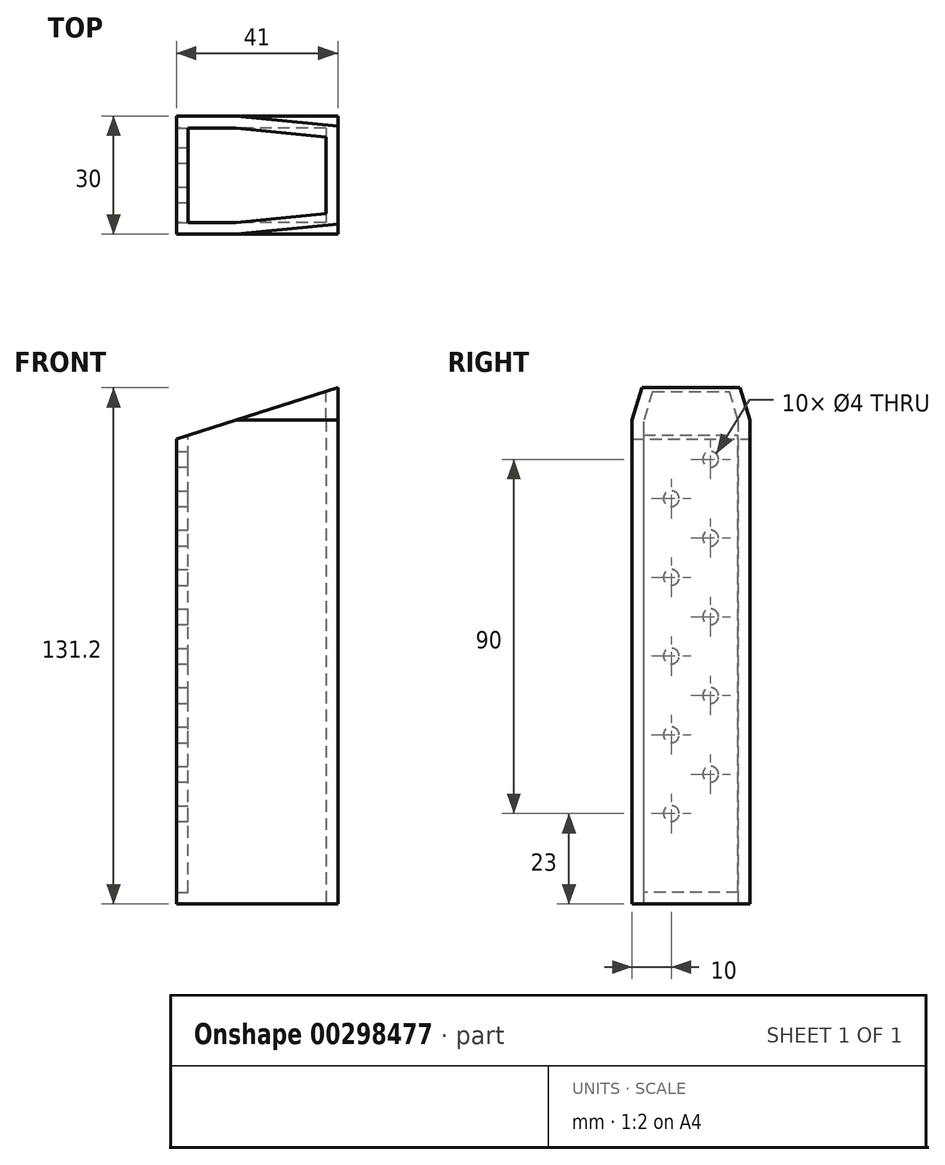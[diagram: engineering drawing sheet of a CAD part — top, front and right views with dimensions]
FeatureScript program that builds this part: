
annotation { "Feature Type Name" : "Feature", "Feature Type Description" : "" }
export const myFeature = defineFeature(function(context is Context, id is Id, definition is map)
    precondition{}
    {
        {
            var Q0;
            Q0=qCreatedBy(makeId("Right.planeOp"),FACE);
            var sketch = newSketch(context, id + "F0", { "sketchPlane" : qUnion([Q0])});
            skLineSegment(sketch, "E0", {"start": v(10, 10) * mm, "end": v(0, 20) * mm});
            skLineSegment(sketch, "E1", {"start": v(0, 20) * mm, "end": v(10, 30) * mm});
            skLineSegment(sketch, "E2", {"start": v(10, 30) * mm, "end": v(0, 40) * mm});
            skLineSegment(sketch, "E3", {"start": v(0, 40) * mm, "end": v(10, 50) * mm});
            skLineSegment(sketch, "E4", {"start": v(10, 50) * mm, "end": v(0, 60) * mm});
            skLineSegment(sketch, "E5", {"start": v(0, 60) * mm, "end": v(10, 70) * mm});
            skLineSegment(sketch, "E6", {"start": v(10, 70) * mm, "end": v(0, 80) * mm});
            skLineSegment(sketch, "E7", {"start": v(0, 80) * mm, "end": v(10, 90) * mm});
            skLineSegment(sketch, "E8", {"start": v(10, 90) * mm, "end": v(0, 100) * mm});
            skCircle(sketch, "E9", {"center": v(10, 90) * mm, "radius": 2 * mm});
            skCircle(sketch, "E10", {"center": v(0, 80) * mm, "radius": 2 * mm});
            skCircle(sketch, "E11", {"center": v(10, 70) * mm, "radius": 2 * mm});
            skCircle(sketch, "E12", {"center": v(0, 60) * mm, "radius": 2 * mm});
            skCircle(sketch, "E13", {"center": v(10, 50) * mm, "radius": 2 * mm});
            skCircle(sketch, "E14", {"center": v(0, 40) * mm, "radius": 2 * mm});
            skCircle(sketch, "E15", {"center": v(10, 30) * mm, "radius": 2 * mm});
            skCircle(sketch, "E16", {"center": v(0, 20) * mm, "radius": 2 * mm});
            skCircle(sketch, "E17", {"center": v(10, 10) * mm, "radius": 2 * mm});
            skCircle(sketch, "E18", {"center": v(0, 0) * mm, "radius": 2 * mm});
            skLineSegment(sketch, "E19", {"start": v(0, 100) * mm, "end": v(0, 80) * mm});
            skLineSegment(sketch, "E20", {"start": v(0, 60) * mm, "end": v(0, 80) * mm});
            skLineSegment(sketch, "E21", {"start": v(0, 60) * mm, "end": v(0, 40) * mm});
            skLineSegment(sketch, "E22", {"start": v(0, 40) * mm, "end": v(0, 20) * mm});
            skLineSegment(sketch, "E23", {"start": v(0, 20) * mm, "end": v(0, 0) * mm});
            skLineSegment(sketch, "E24", {"start": v(10, 10) * mm, "end": v(0, 0) * mm});
            skLineSegment(sketch, "E25", {"start": v(10, 10) * mm, "end": v(10, 30) * mm});
            skLineSegment(sketch, "E26", {"start": v(10, 90) * mm, "end": v(10, 70) * mm});
            skLineSegment(sketch, "E27", {"start": v(10, 70) * mm, "end": v(10, 50) * mm});
            skLineSegment(sketch, "E28", {"start": v(10, 50) * mm, "end": v(10, 30) * mm});
            skLineSegment(sketch, "E29", {"start": v(10, 0) * mm, "end": v(10, 10) * mm});
            skLineSegment(sketch, "E30", {"start": v(5, -20) * mm, "end": v(-7, -20) * mm});
            skLineSegment(sketch, "E31", {"start": v(5, -20) * mm, "end": v(17, -20) * mm});
            skLineSegment(sketch, "E32", {"start": v(5, 0) * mm, "end": v(5, -20) * mm});
            skCircle(sketch, "E33", {"center": v(0, 100) * mm, "radius": 2 * mm});
            skLineSegment(sketch, "E34", {"start": v(5, 0) * mm, "end": v(10, 0) * mm});
            skLineSegment(sketch, "E35", {"start": v(5, 0) * mm, "end": v(0, 0) * mm});
            skLineSegment(sketch, "E36", {"start": v(-7, -20) * mm, "end": v(-7, 100) * mm});
            skLineSegment(sketch, "E37", {"start": v(17, -20) * mm, "end": v(17, 100) * mm});
            skLineSegment(sketch, "E38", {"start": v(17, 100) * mm, "end": v(14, 109.54) * mm});
            skLineSegment(sketch, "E39", {"start": v(14, 109.54) * mm, "end": v(-4, 109.54) * mm});
            skLineSegment(sketch, "E40", {"start": v(-4, 109.54) * mm, "end": v(-7, 100) * mm});
            skSolve(sketch);
        }
        {
            var Q0;
            Q0 = qSketchRegion(id + "F0", true);
            var Q1;
            {var subQ5=sQuery(id+"F0.wireOp",EDGE,"E17");var subQ6=sQuery(id+"F0.wireOp",EDGE,"E0");var subQ7=makeQuery(id+"F0.imprint","INTERSECT",VERTEX,{"derivedFrom":[subQ6,subQ5]});Q1=makeQuery(id+"F0.imprint","IMPRINT",FACE,{"disambiguationData":[TD([[makeQuery(id+"F0.imprint","IMPRINT",EDGE,{"disambiguationData":[TD([[subQ7,-1.0]])],"derivedFrom":subQ6}),1.0]])]});}
            var Q2;
            {var subQ7=sQuery(id+"F0.wireOp",EDGE,"E34");Q2=makeQuery(id+"F0.imprint","IMPRINT",FACE,{"disambiguationData":[TD([[makeQuery(id+"F0.imprint","IMPRINT",EDGE,{"derivedFrom":subQ7}),1.0]])]});}
            var Q3;
            {var subQ1=sQuery(id+"F0.wireOp",EDGE,"E0");var subQ9=sQuery(id+"F0.wireOp",EDGE,"E17");var subQ10=makeQuery(id+"F0.imprint","INTERSECT",VERTEX,{"derivedFrom":[subQ1,subQ9]});Q3=makeQuery(id+"F0.imprint","IMPRINT",FACE,{"disambiguationData":[TD([[makeQuery(id+"F0.imprint","IMPRINT",EDGE,{"disambiguationData":[TD([[subQ10,-1.0]])],"derivedFrom":subQ1}),-1.0]])]});}
            var Q4;
            {var subQ1=sQuery(id+"F0.wireOp",EDGE,"E1");var subQ9=sQuery(id+"F0.wireOp",EDGE,"E16");var subQ10=makeQuery(id+"F0.imprint","INTERSECT",VERTEX,{"derivedFrom":[subQ1,subQ9]});Q4=makeQuery(id+"F0.imprint","IMPRINT",FACE,{"disambiguationData":[TD([[makeQuery(id+"F0.imprint","IMPRINT",EDGE,{"disambiguationData":[TD([[subQ10,-1.0]])],"derivedFrom":subQ1}),1.0]])]});}
            var Q5;
            {var subQ1=sQuery(id+"F0.wireOp",EDGE,"E2");var subQ8=sQuery(id+"F0.wireOp",EDGE,"E15");var subQ11=makeQuery(id+"F0.imprint","INTERSECT",VERTEX,{"derivedFrom":[subQ1,subQ8]});Q5=makeQuery(id+"F0.imprint","IMPRINT",FACE,{"disambiguationData":[TD([[makeQuery(id+"F0.imprint","IMPRINT",EDGE,{"disambiguationData":[TD([[subQ11,-1.0]])],"derivedFrom":subQ1}),-1.0]])]});}
            var Q6;
            {var subQ1=sQuery(id+"F0.wireOp",EDGE,"E3");var subQ5=sQuery(id+"F0.wireOp",EDGE,"E14");var subQ6=makeQuery(id+"F0.imprint","INTERSECT",VERTEX,{"derivedFrom":[subQ1,subQ5]});Q6=makeQuery(id+"F0.imprint","IMPRINT",FACE,{"disambiguationData":[TD([[makeQuery(id+"F0.imprint","IMPRINT",EDGE,{"disambiguationData":[TD([[subQ6,-1.0]])],"derivedFrom":subQ1}),1.0]])]});}
            var Q7;
            {var subQ1=sQuery(id+"F0.wireOp",EDGE,"E4");var subQ9=sQuery(id+"F0.wireOp",EDGE,"E13");var subQ10=makeQuery(id+"F0.imprint","INTERSECT",VERTEX,{"derivedFrom":[subQ1,subQ9]});Q7=makeQuery(id+"F0.imprint","IMPRINT",FACE,{"disambiguationData":[TD([[makeQuery(id+"F0.imprint","IMPRINT",EDGE,{"disambiguationData":[TD([[subQ10,-1.0]])],"derivedFrom":subQ1}),-1.0]])]});}
            var Q8;
            {var subQ1=sQuery(id+"F0.wireOp",EDGE,"E5");var subQ9=sQuery(id+"F0.wireOp",EDGE,"E12");var subQ10=makeQuery(id+"F0.imprint","INTERSECT",VERTEX,{"derivedFrom":[subQ1,subQ9]});Q8=makeQuery(id+"F0.imprint","IMPRINT",FACE,{"disambiguationData":[TD([[makeQuery(id+"F0.imprint","IMPRINT",EDGE,{"disambiguationData":[TD([[subQ10,-1.0]])],"derivedFrom":subQ1}),1.0]])]});}
            var Q9;
            {var subQ1=sQuery(id+"F0.wireOp",EDGE,"E6");var subQ9=sQuery(id+"F0.wireOp",EDGE,"E11");var subQ10=makeQuery(id+"F0.imprint","INTERSECT",VERTEX,{"derivedFrom":[subQ1,subQ9]});Q9=makeQuery(id+"F0.imprint","IMPRINT",FACE,{"disambiguationData":[TD([[makeQuery(id+"F0.imprint","IMPRINT",EDGE,{"disambiguationData":[TD([[subQ10,-1.0]])],"derivedFrom":subQ1}),-1.0]])]});}
            var Q10;
            {var subQ0=sQuery(id+"F0.wireOp",EDGE,"E10");var subQ1=sQuery(id+"F0.wireOp",EDGE,"E7");var subQ2=makeQuery(id+"F0.imprint","INTERSECT",VERTEX,{"derivedFrom":[subQ1,subQ0]});Q10=makeQuery(id+"F0.imprint","IMPRINT",FACE,{"disambiguationData":[TD([[makeQuery(id+"F0.imprint","IMPRINT",EDGE,{"disambiguationData":[TD([[subQ2,-1.0]])],"derivedFrom":subQ1}),1.0]])]});}
            extrude(context, id + "F1", {"entities" : qUnion([Q0, Q1, Q2, Q3, Q4, Q5, Q6, Q7, Q8, Q9, Q10]), "oppositeDirection" : true, "depth" : 3 * mm});
        }
        {
            var Q0;
            Q0=makeQuery(id+"F1.opExtrude","CAP_FACE",FACE,{"disambiguationData":[OSD([sQuery(id+"F0.wireOp",EDGE,"E9"),sQuery(id+"F0.wireOp",EDGE,"E10"),sQuery(id+"F0.wireOp",EDGE,"E11"),sQuery(id+"F0.wireOp",EDGE,"E12"),sQuery(id+"F0.wireOp",EDGE,"E13"),sQuery(id+"F0.wireOp",EDGE,"E14"),sQuery(id+"F0.wireOp",EDGE,"E15"),sQuery(id+"F0.wireOp",EDGE,"E16"),sQuery(id+"F0.wireOp",EDGE,"E17"),sQuery(id+"F0.wireOp",EDGE,"E18"),sQuery(id+"F0.wireOp",EDGE,"E30"),sQuery(id+"F0.wireOp",EDGE,"E31"),sQuery(id+"F0.wireOp",EDGE,"E33"),sQuery(id+"F0.wireOp",EDGE,"E36"),sQuery(id+"F0.wireOp",EDGE,"E37"),sQuery(id+"F0.wireOp",EDGE,"E38"),sQuery(id+"F0.wireOp",EDGE,"E39"),sQuery(id+"F0.wireOp",EDGE,"E40")])],"isStart":false});
            var sketch = newSketch(context, id + "F2", { "sketchPlane" : qUnion([Q0])});
            skLineSegment(sketch, "E41", {"start": v(-14, 109.54) * mm, "end": v(-17, 109.54) * mm});
            skLineSegment(sketch, "E42", {"start": v(-17, 100) * mm, "end": v(-20, 100) * mm});
            skLineSegment(sketch, "E43", {"start": v(-17, -20) * mm, "end": v(-20, -20) * mm});
            skLineSegment(sketch, "E44", {"start": v(-17, -20) * mm, "end": v(-17, -23) * mm});
            skLineSegment(sketch, "E45", {"start": v(7, -23) * mm, "end": v(10, -23) * mm});
            skLineSegment(sketch, "E46", {"start": v(10, -23) * mm, "end": v(10, 100) * mm});
            skLineSegment(sketch, "E47", {"start": v(4, 109.54) * mm, "end": v(7, 109.54) * mm});
            skLineSegment(sketch, "E48", {"start": v(7, 109.54) * mm, "end": v(10, 100) * mm});
            skLineSegment(sketch, "E49", {"start": v(-17, 109.54) * mm, "end": v(-20, 100) * mm});
            skLineSegment(sketch, "E50", {"start": v(-20, -20) * mm, "end": v(-20, 100) * mm});
            skLineSegment(sketch, "E51", {"start": v(-20, -20) * mm, "end": v(-20, -23) * mm});
            skLineSegment(sketch, "E52", {"start": v(-20, -23) * mm, "end": v(-17, -23) * mm});
            skLineSegment(sketch, "E53", {"start": v(7, -23) * mm, "end": v(7, -20) * mm});
            skSolve(sketch);
        }
        {
            var Q0;
            Q0 = qSketchRegion(id + "F2", true);
            var Q1;
            Q1=makeQuery(id+"F2.imprint","IMPRINT",FACE,{"disambiguationData":[TD([[makeQuery(id+"F2.imprint","IMPRINT",EDGE,{"derivedFrom":sQuery(id+"F2.wireOp",EDGE,"E42")}),1.0]])]});
            var Q2;
            Q2=makeQuery(id+"F2.imprint","IMPRINT",FACE,{"disambiguationData":[TD([[makeQuery(id+"F2.imprint","IMPRINT",EDGE,{"derivedFrom":sQuery(id+"F2.wireOp",EDGE,"E45")}),1.0]])]});
            var Q3;
            Q3=makeQuery(id+"F2.imprint","IMPRINT",FACE,{"disambiguationData":[TD([[makeQuery(id+"F2.imprint","IMPRINT",EDGE,{"derivedFrom":sQuery(id+"F2.wireOp",EDGE,"E41")}),1.0]])]});
            extrude(context, id + "F3", {"entities" : qUnion([Q0, Q1, Q2, Q3]), "operationType" : NewBodyOperationType.ADD, "oppositeDirection" : true, "depth" : 41 * mm, "offsetDistance" : 25 * mm});
        }
        {
            var Q0;
            Q0=makeQuery(id+"F3.opExtrude","CAP_FACE",FACE,{"disambiguationData":[OSD([sQuery(id+"F0.wireOp",EDGE,"E36"),sQuery(id+"F0.wireOp",EDGE,"E40"),sQuery(id+"F2.wireOp",EDGE,"E45"),sQuery(id+"F2.wireOp",EDGE,"E46"),sQuery(id+"F2.wireOp",EDGE,"E47"),sQuery(id+"F2.wireOp",EDGE,"E48"),sQuery(id+"F2.wireOp",EDGE,"E53")])],"isStart":false});
            var sketch = newSketch(context, id + "F4", { "sketchPlane" : qUnion([Q0])});
            skLineSegment(sketch, "E54", {"start": v(-7, 109.54) * mm, "end": v(-10, 100) * mm});
            skLineSegment(sketch, "E55", {"start": v(-10, 100) * mm, "end": v(-10, -23) * mm});
            skLineSegment(sketch, "E56", {"start": v(-10, -23) * mm, "end": v(20, -23) * mm});
            skLineSegment(sketch, "E57", {"start": v(20, -23) * mm, "end": v(20, 100) * mm});
            skLineSegment(sketch, "E58", {"start": v(20, 100) * mm, "end": v(17, 109.54) * mm});
            skLineSegment(sketch, "E59", {"start": v(17, 109.54) * mm, "end": v(-7, 109.54) * mm});
            skSolve(sketch);
        }
        {
            var Q0;
            Q0 = qSketchRegion(id + "F4", true);
            extrude(context, id + "F5", {"entities" : qUnion([Q0]), "operationType" : NewBodyOperationType.ADD, "oppositeDirection" : true, "depth" : 3 * mm, "offsetDistance" : 25 * mm});
        }
        {
            var Q0;
            Q0=makeQuery(id+"F3.opExtrude","SWEPT_FACE",FACE,{"disambiguationData":[OSD([sQuery(id+"F2.wireOp",EDGE,"E50"),sQuery(id+"F2.wireOp",EDGE,"E51")])]});
            var sketch = newSketch(context, id + "F6", { "sketchPlane" : qUnion([Q0])});
            skLineSegment(sketch, "E60", {"start": v(3, 100) * mm, "end": v(3, 110) * mm});
            skLineSegment(sketch, "E61", {"start": v(3, 110) * mm, "end": v(-38, 110) * mm});
            skLineSegment(sketch, "E62", {"start": v(-38, 110) * mm, "end": v(-38, 108.2) * mm});
            skLineSegment(sketch, "E63", {"start": v(-38, 108.2) * mm, "end": v(3, 95.2) * mm});
            skLineSegment(sketch, "E64", {"start": v(3, 95.2) * mm, "end": v(3, 100) * mm});
            skSolve(sketch);
        }
        {
            var Q0;
            Q0 = qSketchRegion(id + "F6", true);
            extrude(context, id + "F7", {"entities" : qUnion([Q0]), "operationType" : NewBodyOperationType.REMOVE, "oppositeDirection" : true, "depth" : 39.6 * mm, "offsetDistance" : 25 * mm});
        }
    });
